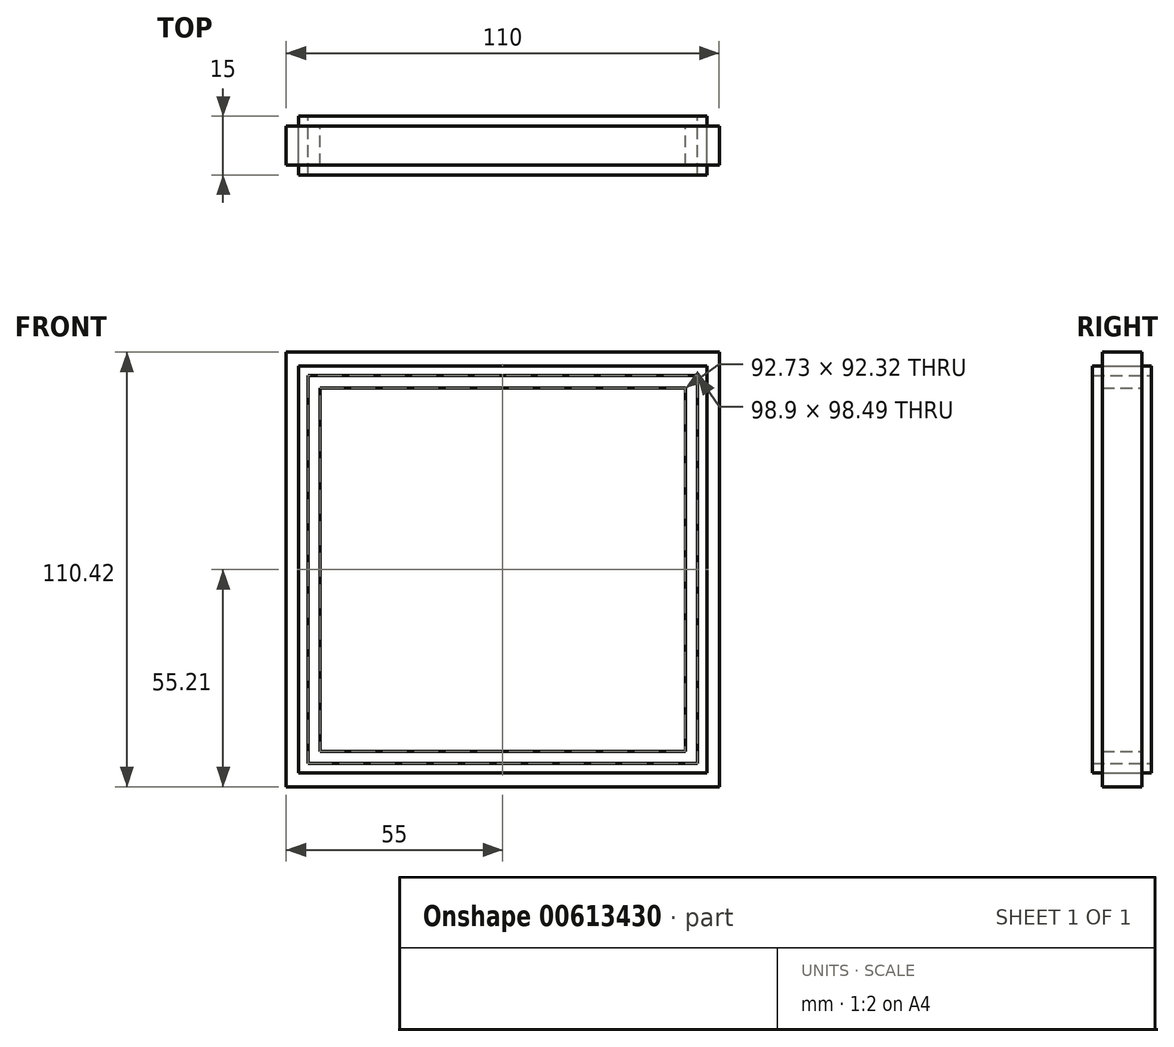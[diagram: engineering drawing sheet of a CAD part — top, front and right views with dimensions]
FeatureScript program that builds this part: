
annotation { "Feature Type Name" : "Feature", "Feature Type Description" : "" }
export const myFeature = defineFeature(function(context is Context, id is Id, definition is map)
    precondition{}
    {
        {
            var Q0;
            Q0=qCreatedBy(makeId("Front.planeOp"),FACE);
            var sketch = newSketch(context, id + "F0", { "sketchPlane" : qUnion([Q0])});
            skLineSegment(sketch, "E0.bottom", {"start": v(-55, 55.2) * mm, "end": v(55, 55.2) * mm});
            skLineSegment(sketch, "E0.top", {"start": v(-55, -55.2) * mm, "end": v(55, -55.2) * mm});
            skLineSegment(sketch, "E0.left", {"start": v(-55, 55.2) * mm, "end": v(-55, -55.2) * mm});
            skLineSegment(sketch, "E0.right", {"start": v(55, 55.2) * mm, "end": v(55, -55.2) * mm});
            skPoint(sketch, "E0.middle", {"position": v(0, 0) * mm});
            skLineSegment(sketch, "E1.bottom", {"start": v(-51.92, 51.71) * mm, "end": v(51.92, 51.71) * mm});
            skLineSegment(sketch, "E1.top", {"start": v(-51.92, -51.71) * mm, "end": v(51.92, -51.71) * mm});
            skLineSegment(sketch, "E1.left", {"start": v(-51.92, 51.71) * mm, "end": v(-51.92, -51.71) * mm});
            skLineSegment(sketch, "E1.right", {"start": v(51.92, 51.71) * mm, "end": v(51.92, -51.71) * mm});
            skLineSegment(sketch, "E2.bottom", {"start": v(-49.45, 49.24) * mm, "end": v(49.45, 49.24) * mm});
            skLineSegment(sketch, "E2.top", {"start": v(-49.45, -49.24) * mm, "end": v(49.45, -49.24) * mm});
            skLineSegment(sketch, "E2.left", {"start": v(-49.45, 49.24) * mm, "end": v(-49.45, -49.24) * mm});
            skLineSegment(sketch, "E2.right", {"start": v(49.45, 49.24) * mm, "end": v(49.45, -49.24) * mm});
            skLineSegment(sketch, "E3.bottom", {"start": v(-46.37, 46.16) * mm, "end": v(46.37, 46.16) * mm});
            skLineSegment(sketch, "E3.top", {"start": v(-46.37, -46.16) * mm, "end": v(46.37, -46.16) * mm});
            skLineSegment(sketch, "E3.left", {"start": v(-46.37, 46.16) * mm, "end": v(-46.37, -46.16) * mm});
            skLineSegment(sketch, "E3.right", {"start": v(46.37, 46.16) * mm, "end": v(46.37, -46.16) * mm});
            skSolve(sketch);
        }
        {
            var Q0;
            Q0=makeQuery(id+"F0.imprint","IMPRINT",FACE,{"disambiguationData":[TD([[makeQuery(id+"F0.imprint","IMPRINT",EDGE,{"derivedFrom":sQuery(id+"F0.wireOp",EDGE,"E1.bottom")}),-1.0]])]});
            extrude(context, id + "F1", {"entities" : qUnion([Q0]), "endBound" : BoundingType.SYMMETRIC, "depth" : 15 * mm, "offsetDistance" : 25 * mm});
        }
        {
            var Q0;
            Q0=makeQuery(id+"F0.imprint","IMPRINT",FACE,{"disambiguationData":[TD([[makeQuery(id+"F0.imprint","IMPRINT",EDGE,{"derivedFrom":sQuery(id+"F0.wireOp",EDGE,"E0.bottom")}),-1.0]])]});
            var Q1;
            Q1=makeQuery(id+"F0.imprint","IMPRINT",FACE,{"disambiguationData":[TD([[makeQuery(id+"F0.imprint","IMPRINT",EDGE,{"derivedFrom":sQuery(id+"F0.wireOp",EDGE,"E1.bottom")}),-1.0]])]});
            var Q2;
            Q2=makeQuery(id+"F0.imprint","IMPRINT",FACE,{"disambiguationData":[TD([[makeQuery(id+"F0.imprint","IMPRINT",EDGE,{"derivedFrom":sQuery(id+"F0.wireOp",EDGE,"E2.bottom")}),-1.0]])]});
            extrude(context, id + "F2", {"entities" : qUnion([Q0, Q1, Q2]), "endBound" : BoundingType.SYMMETRIC, "depth" : 10 * mm, "offsetDistance" : 25 * mm});
        }
    });
